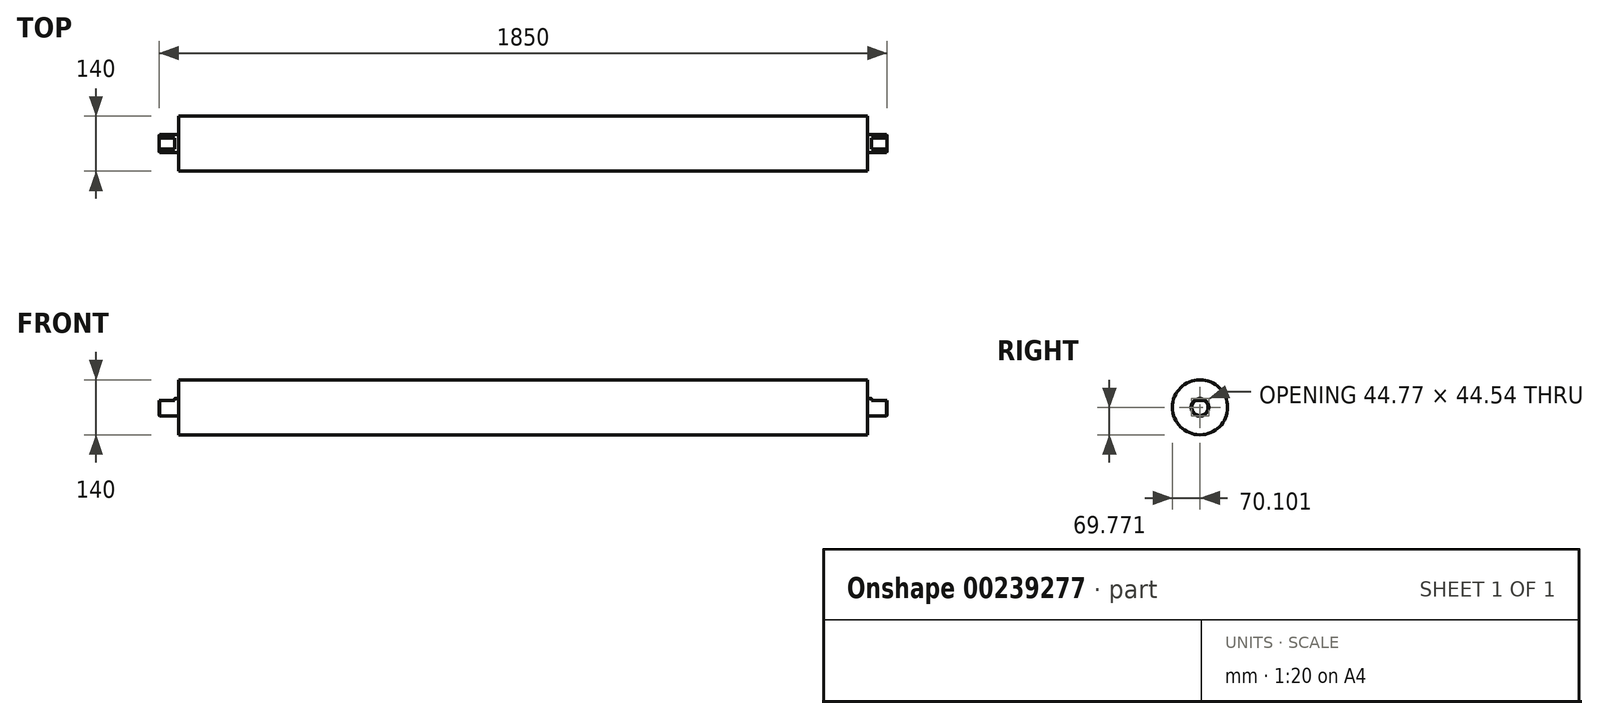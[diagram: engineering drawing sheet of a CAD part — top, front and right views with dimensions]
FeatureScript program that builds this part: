
annotation { "Feature Type Name" : "Feature", "Feature Type Description" : "" }
export const myFeature = defineFeature(function(context is Context, id is Id, definition is map)
    precondition{}
    {
        {
            var Q0;
            Q0=qCreatedBy(makeId("Right.planeOp"),FACE);
            var sketch = newSketch(context, id + "F0", { "sketchPlane" : qUnion([Q0])});
            skCircle(sketch, "E0", {"center": v(0, 0) * mm, "radius": 27.5 * mm});
            skSolve(sketch);
        }
        {
            var Q0;
            Q0 = qSketchRegion(id + "F0", true);
            extrude(context, id + "F1", {"entities" : qUnion([Q0]), "endBound" : BoundingType.SYMMETRIC, "depth" : 1750 * mm});
        }
        {
            var Q0;
            Q0=makeQuery(id+"F1.opExtrude","CAP_FACE",FACE,{"disambiguationData":[OSD([sQuery(id+"F0.wireOp",EDGE,"E0")])],"isStart":false});
            var sketch = newSketch(context, id + "F2", { "sketchPlane" : qUnion([Q0])});
            skCircle(sketch, "E1.0.0", {"center": v(0, 0) * mm, "radius": 27.5 * mm, "construction": true});
            skCircle(sketch, "E2", {"center": v(0, 0) * mm, "radius": 22.5 * mm});
            skSolve(sketch);
        }
        {
            var Q0;
            Q0=makeQuery(id+"F2.imprint","IMPRINT",FACE,{"disambiguationData":[TD([[makeQuery(id+"F2.imprint","IMPRINT",EDGE,{"derivedFrom":sQuery(id+"F2.wireOp",EDGE,"E2")}),1.0]])]});
            extrude(context, id + "F3", {"entities" : qUnion([Q0]), "depth" : 50 * mm});
        }
        {
            var Q0;
            Q0=makeQuery(id+"F3.opExtrude","CAP_FACE",FACE,{"disambiguationData":[OSD([sQuery(id+"F2.wireOp",EDGE,"E2")])],"isStart":false});
            var sketch = newSketch(context, id + "F4", { "sketchPlane" : qUnion([Q0])});
            skArc(sketch, "E3.0.0", {"start": v(14.14, 17.5) * mm, "mid": v(0, 22.5) * mm, "end": v(-14.14, 17.5) * mm});
            skLineSegment(sketch, "E4", {"start": v(0, 0) * mm, "end": v(0, 22.5) * mm, "construction": true});
            skLineSegment(sketch, "E5", {"start": v(0, 22.5) * mm, "end": v(35.81, 22.5) * mm, "construction": true});
            skLineSegment(sketch, "E6.0", {"start": v(-14.14, 17.5) * mm, "end": v(14.14, 17.5) * mm});
            skSolve(sketch);
        }
        {
            var Q0;
            Q0 = qSketchRegion(id + "F4", true);
            extrude(context, id + "F5", {"entities" : qUnion([Q0]), "operationType" : NewBodyOperationType.REMOVE, "oppositeDirection" : true, "depth" : 40 * mm});
        }
        {
            var Q0;
            Q0=makeQuery(id+"F3.opExtrude","CAP_EDGE",EDGE,{"disambiguationData":[OSD([sQuery(id+"F2.wireOp",EDGE,"E2")])],"isStart":false});
            chamfer(context, id + "F6", {"entities" : qUnion([Q0]), "width" : 2 * mm, "tangentPropagation" : true});
        }
        {
            var Q0;
            Q0=makeQuery(id+"F3.opExtrude","SWEPT_BODY",BODY,{"disambiguationData":[OSD([sQuery(id+"F2.wireOp",EDGE,"E2")])]});
            var Q1;
            Q1=qCreatedBy(makeId("Right.planeOp"),FACE);
            mirror(context, id + "F7", {"operationType" : NewBodyOperationType.ADD, "entities" : qUnion([Q0]), "mirrorPlane" : qUnion([Q1])});
        }
        {
            var Q0;
            Q0=qCreatedBy(makeId("Right.planeOp"),FACE);
            var sketch = newSketch(context, id + "F8", { "sketchPlane" : qUnion([Q0])});
            skCircle(sketch, "E7", {"center": v(0, 0) * mm, "radius": 70 * mm});
            skSolve(sketch);
        }
        {
            var Q0;
            Q0 = qSketchRegion(id + "F8", true);
            extrude(context, id + "F9", {"entities" : qUnion([Q0]), "operationType" : NewBodyOperationType.ADD, "endBound" : BoundingType.SYMMETRIC, "depth" : 1750 * mm});
        }
    });
